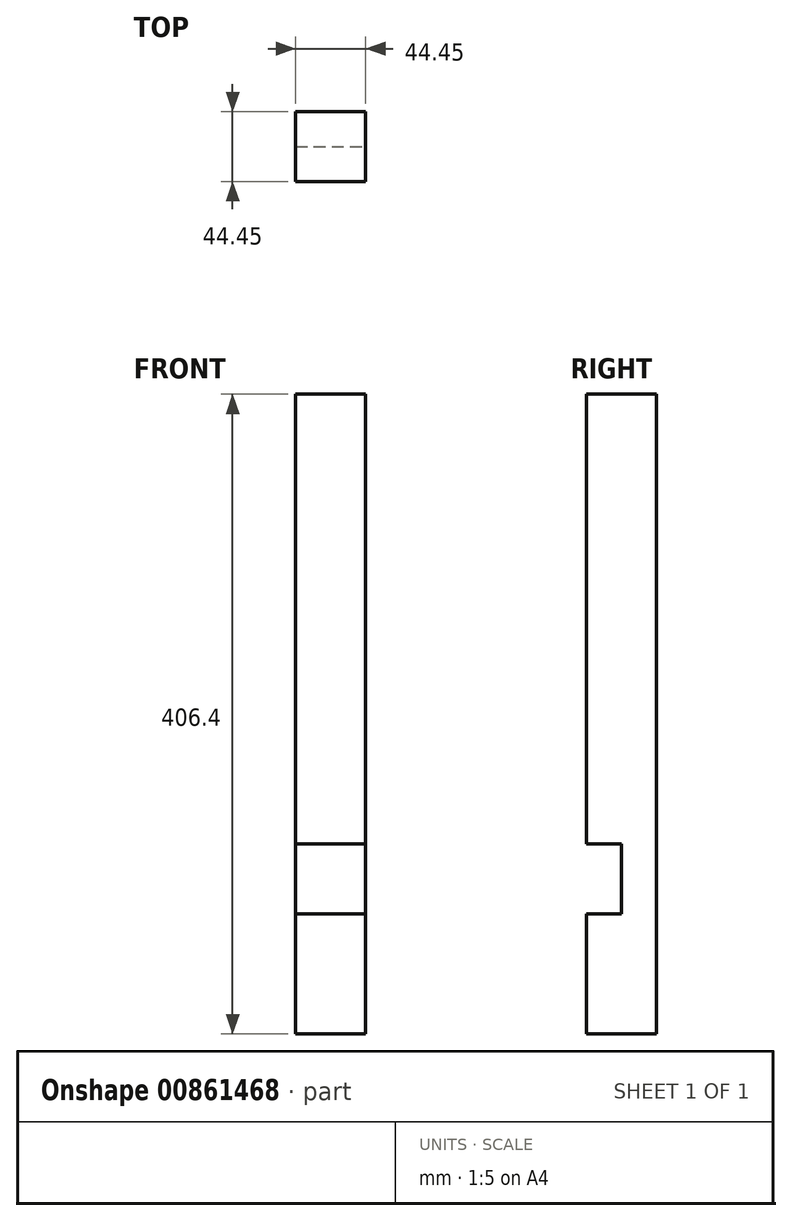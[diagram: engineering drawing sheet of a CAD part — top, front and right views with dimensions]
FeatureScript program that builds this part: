
annotation { "Feature Type Name" : "Feature", "Feature Type Description" : "" }
export const myFeature = defineFeature(function(context is Context, id is Id, definition is map)
    precondition{}
    {
        {
            var Q0;
            Q0=qCreatedBy(makeId("Top.planeOp"),FACE);
            var sketch = newSketch(context, id + "F0", { "sketchPlane" : qUnion([Q0])});
            skLineSegment(sketch, "E0.bottom", {"start": v(0, 0) * mm, "end": v(44.45, 0) * mm});
            skLineSegment(sketch, "E0.top", {"start": v(0, -44.45) * mm, "end": v(44.45, -44.45) * mm});
            skLineSegment(sketch, "E0.left", {"start": v(0, 0) * mm, "end": v(0, -44.45) * mm});
            skLineSegment(sketch, "E0.right", {"start": v(44.45, 0) * mm, "end": v(44.45, -44.45) * mm});
            skSolve(sketch);
        }
        {
            var Q0;
            Q0 = qSketchRegion(id + "F0", true);
            extrude(context, id + "F1", {"entities" : qUnion([Q0]), "depth" : 406.4 * mm, "offsetDistance" : 25.4 * mm});
        }
        {
            var Q0;
            Q0=makeQuery(id+"F1.opExtrude","SWEPT_FACE",FACE,{"disambiguationData":[OSD([sQuery(id+"F0.wireOp",EDGE,"E0.top")])]});
            var sketch = newSketch(context, id + "F2", { "sketchPlane" : qUnion([Q0])});
            skLineSegment(sketch, "E1.bottom", {"start": v(0, 76.2) * mm, "end": v(44.45, 76.2) * mm});
            skLineSegment(sketch, "E1.top", {"start": v(0, 120.65) * mm, "end": v(44.45, 120.65) * mm});
            skLineSegment(sketch, "E1.left", {"start": v(0, 76.2) * mm, "end": v(0, 120.65) * mm});
            skLineSegment(sketch, "E1.right", {"start": v(44.45, 76.2) * mm, "end": v(44.45, 120.65) * mm});
            skSolve(sketch);
        }
        {
            var Q0;
            Q0=makeQuery(id+"F2.imprint","IMPRINT",FACE,{"disambiguationData":[TD([[makeQuery(id+"F2.imprint","IMPRINT",EDGE,{"derivedFrom":sQuery(id+"F2.wireOp",EDGE,"E1.bottom")}),1.0]])]});
            extrude(context, id + "F3", {"entities" : qUnion([Q0]), "operationType" : NewBodyOperationType.REMOVE, "oppositeDirection" : true, "depth" : 22.22 * mm, "offsetDistance" : 25.4 * mm});
        }
    });
